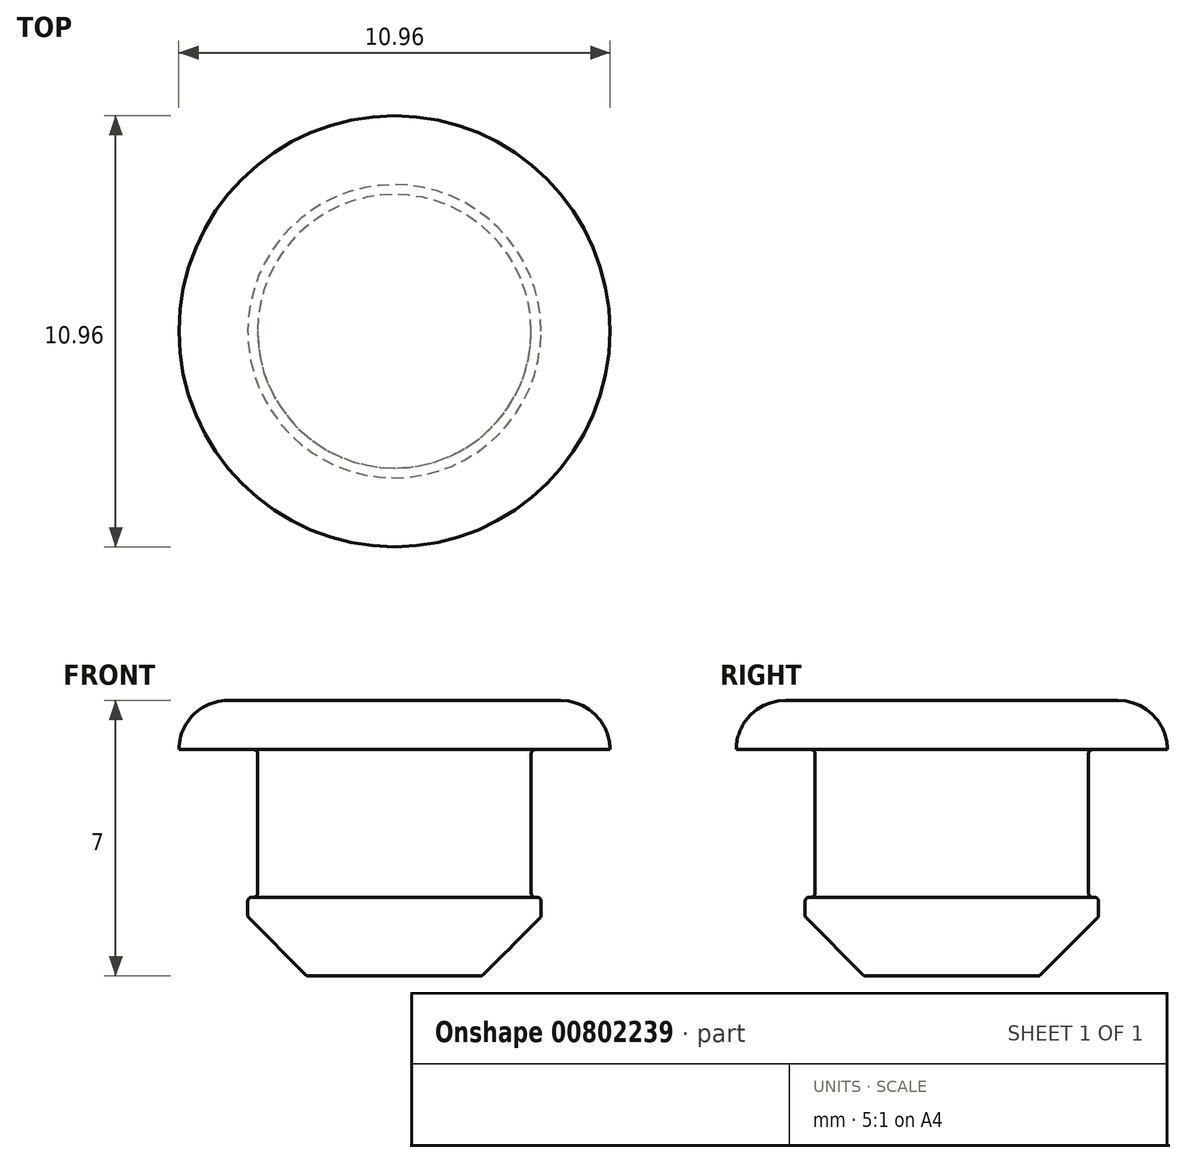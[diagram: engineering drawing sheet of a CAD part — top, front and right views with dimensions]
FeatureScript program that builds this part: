
annotation { "Feature Type Name" : "Feature", "Feature Type Description" : "" }
export const myFeature = defineFeature(function(context is Context, id is Id, definition is map)
    precondition{}
    {
        {
            var Q0;
            Q0=qCreatedBy(makeId("Front.planeOp"),FACE);
            var sketch = newSketch(context, id + "F0", { "sketchPlane" : qUnion([Q0])});
            skLineSegment(sketch, "E0", {"start": v(0, 0) * mm, "end": v(-5.48, 0) * mm});
            skLineSegment(sketch, "E1", {"start": v(-5.48, 0) * mm, "end": v(-5.48, -1.25) * mm});
            skLineSegment(sketch, "E2", {"start": v(-5.48, -1.25) * mm, "end": v(-3.48, -1.25) * mm});
            skLineSegment(sketch, "E3", {"start": v(-3.48, -1.25) * mm, "end": v(-3.48, -5) * mm});
            skLineSegment(sketch, "E4", {"start": v(-3.48, -5) * mm, "end": v(-3.73, -5) * mm});
            skLineSegment(sketch, "E5", {"start": v(-3.73, -5) * mm, "end": v(-3.73, -7) * mm});
            skLineSegment(sketch, "E6", {"start": v(-3.73, -7) * mm, "end": v(0, -7) * mm});
            skLineSegment(sketch, "E7", {"start": v(0, -7) * mm, "end": v(0, 0) * mm});
            skSolve(sketch);
        }
        {
            var Q0;
            Q0=makeQuery(id+"F0.imprint","IMPRINT",FACE,{"disambiguationData":[TD([[makeQuery(id+"F0.imprint","IMPRINT",EDGE,{"derivedFrom":sQuery(id+"F0.wireOp",EDGE,"E0")}),1.0]])]});
            var Q1;
            Q1=sQuery(id+"F0.wireOp",EDGE,"E7");
            revolve(context, id + "F1", {"surfaceOperationType" : NewSurfaceOperationType.NEW, "entities" : qUnion([Q0]), "axis" : qUnion([Q1]), "revolveType" : RevolveType.FULL});
        }
        {
            var Q0;
            Q0=makeQuery(id+"F1.opRevolve","SWEPT_EDGE",EDGE,{"disambiguationData":[OSD([sQuery(id+"F0.wireOp",EDGE,"E0"),sQuery(id+"F0.wireOp",EDGE,"E1")])]});
            fillet(context, id + "F2", {"entities" : qUnion([Q0]), "tangentPropagation" : true, "radius" : 1.25 * mm, "defaultsChanged" : true, "vertexSettings" : [], "allowEdgeOverflow" : false});
        }
        {
            var Q0;
            Q0=makeQuery(id+"F1.opRevolve","SWEPT_EDGE",EDGE,{"disambiguationData":[OSD([sQuery(id+"F0.wireOp",EDGE,"E5"),sQuery(id+"F0.wireOp",EDGE,"E6")])]});
            chamfer(context, id + "F3", {"entities" : qUnion([Q0]), "width" : 1.5 * mm, "tangentPropagation" : true});
        }
        {
            var Q0;
            Q0=makeQuery(id+"F1.opRevolve","SWEPT_EDGE",EDGE,{"disambiguationData":[OSD([sQuery(id+"F0.wireOp",EDGE,"E4"),sQuery(id+"F0.wireOp",EDGE,"E5")])]});
            var Q1;
            {var subQ0=sQuery(id+"F0.wireOp",EDGE,"E6");Q1=makeQuery(id+"F3.opChamfer","BLEND_EDGE",EDGE,{"blendedFrom":[makeQuery(id+"F1.opRevolve","SWEPT_EDGE",EDGE,{"disambiguationData":[OSD([sQuery(id+"F0.wireOp",EDGE,"E5"),subQ0])]}),makeQuery(id+"F1.opRevolve","SWEPT_FACE",FACE,{"disambiguationData":[OSD([subQ0])]})],"blendedInto":[makeQuery(id+"F1.opRevolve","SWEPT_FACE",FACE,{"disambiguationData":[OSD([subQ0])]})]});}
            var Q2;
            Q2=makeQuery(id+"F1.opRevolve","SWEPT_EDGE",EDGE,{"disambiguationData":[OSD([sQuery(id+"F0.wireOp",EDGE,"E3"),sQuery(id+"F0.wireOp",EDGE,"E4")])]});
            var Q3;
            Q3=makeQuery(id+"F1.opRevolve","SWEPT_EDGE",EDGE,{"disambiguationData":[OSD([sQuery(id+"F0.wireOp",EDGE,"E2"),sQuery(id+"F0.wireOp",EDGE,"E3")])]});
            var Q4;
            Q4=makeQuery(id+"F1.opRevolve","SWEPT_EDGE",EDGE,{"disambiguationData":[OSD([sQuery(id+"F0.wireOp",EDGE,"E1"),sQuery(id+"F0.wireOp",EDGE,"E2")])]});
            var Q5;
            {var subQ0=sQuery(id+"F0.wireOp",EDGE,"E5");Q5=makeQuery(id+"F3.opChamfer","BLEND_EDGE",EDGE,{"blendedFrom":[makeQuery(id+"F1.opRevolve","SWEPT_EDGE",EDGE,{"disambiguationData":[OSD([subQ0,sQuery(id+"F0.wireOp",EDGE,"E6")])]}),makeQuery(id+"F1.opRevolve","SWEPT_FACE",FACE,{"disambiguationData":[OSD([subQ0])]})],"blendedInto":[makeQuery(id+"F1.opRevolve","SWEPT_FACE",FACE,{"disambiguationData":[OSD([subQ0])]})]});}
            fillet(context, id + "F4", {"entities" : qUnion([Q0, Q1, Q2, Q3, Q4, Q5]), "tangentPropagation" : true, "radius" : 0.1 * mm, "defaultsChanged" : false, "vertexSettings" : [], "allowEdgeOverflow" : false});
        }
    });
